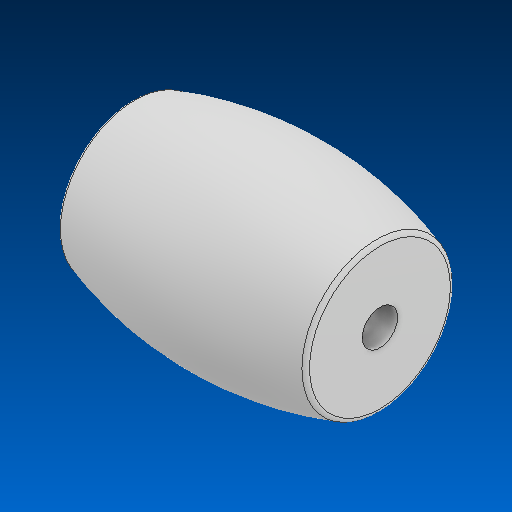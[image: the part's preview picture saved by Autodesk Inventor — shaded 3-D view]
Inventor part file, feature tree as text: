
AUTODESK INVENTOR PART (.ipt)
format: ipt  version: 2022.2 (Build 262287000, 287)  size: 133,120 bytes
history: native  units: in
note: dims shown in document units (in); Inventor stores cm internally (conversion verified against a paired STEP export)
features: fillet x1
ambient origin geometry x8: Origin, YZ Plane, XZ Plane, XY Plane, X Axis, Y Axis, Z Axis, Center Point
bodies: Solid1 (feature_tree)
feature tree (1):
  fillet  "Fillet2"  [1 undecoded]
note: 1 required parameter value undecoded (feature->parameter linkage not recoverable at this tier; creation-order binding heuristic only, values carry confidence <= 0.55)
